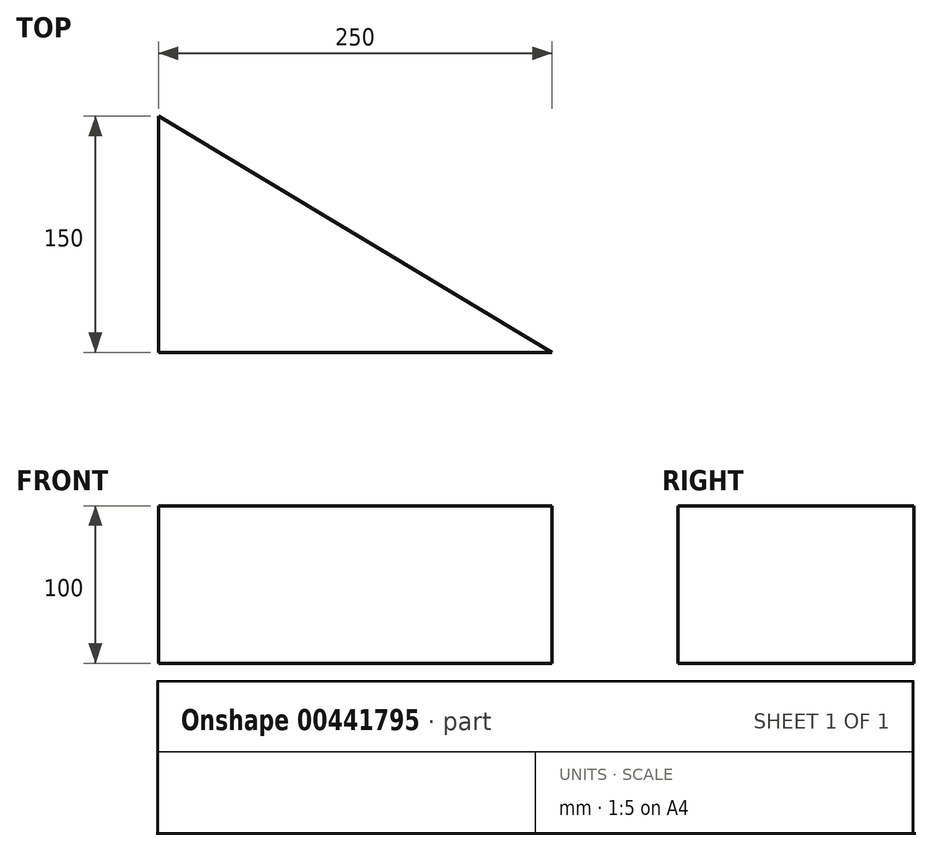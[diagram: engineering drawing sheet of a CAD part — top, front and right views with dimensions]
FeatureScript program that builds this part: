
annotation { "Feature Type Name" : "Feature", "Feature Type Description" : "" }
export const myFeature = defineFeature(function(context is Context, id is Id, definition is map)
    precondition{}
    {
        {
            var Q0;
            Q0=qCreatedBy(makeId("Top.planeOp"),FACE);
            var sketch = newSketch(context, id + "F0", { "sketchPlane" : qUnion([Q0])});
            skLineSegment(sketch, "E0", {"start": v(-115.87, -72.7) * mm, "end": v(134.13, -72.7) * mm});
            skLineSegment(sketch, "E1", {"start": v(134.13, -72.7) * mm, "end": v(134.13, 77.3) * mm});
            skLineSegment(sketch, "E2", {"start": v(134.13, 77.3) * mm, "end": v(-115.87, 77.3) * mm});
            skLineSegment(sketch, "E3", {"start": v(-115.87, 77.3) * mm, "end": v(-115.87, -72.7) * mm});
            skLineSegment(sketch, "E4", {"start": v(-115.87, 77.3) * mm, "end": v(134.13, -72.7) * mm});
            skText(sketch, "E5", { "text": "This way up", "fontName": "OpenSans-Bold.ttf"});
            const initialGuessF0  = {"E5": [0, 0.0346, 1, 0, 0.00947]};
            skSetInitialGuess(sketch, initialGuessF0);
            skSolve(sketch);
        }
        {
            var Q0;
            Q0=makeQuery(id+"F0.imprint","IMPRINT",FACE,{"disambiguationData":[TD([[makeQuery(id+"F0.imprint","IMPRINT",EDGE,{"derivedFrom":sQuery(id+"F0.wireOp",EDGE,"E0")}),1.0]])]});
            extrude(context, id + "F1", {"entities" : qUnion([Q0]), "depth" : 100 * mm});
        }
    });
